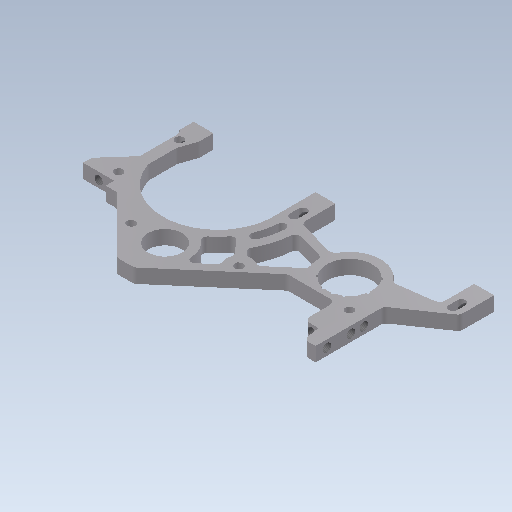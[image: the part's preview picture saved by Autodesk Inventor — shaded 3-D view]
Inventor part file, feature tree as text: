
AUTODESK INVENTOR PART (.ipt)
format: ipt  version: 2020 (Build 240168000, 168)  size: 531,968 bytes
history: native  units: mm (DEFAULTED — no unit token found)
features: sketch x12, hole x8, thread x8, extrude x5, fillet x3, imported_body x1
ambient origin geometry x8: Origin, YZ Plane, XZ Plane, XY Plane, X Axis, Y Axis, Z Axis, Center Point
bodies: Solid1 (feature_tree)
feature tree (37):
  extrude  "Extrusion1"  Depth=2.0mm
  fillet  "Fillet1"  Radius=3.0mm
  extrude  "Extrusion2"  Depth=3.0mm
  fillet  "Fillet2"  Radius=3.0mm
  hole  "Hole1"  [1 undecoded]
  thread  "Thread1"  [1 undecoded]
  hole  "Hole2"  [1 undecoded]
  thread  "Thread2"  [1 undecoded]
  extrude  "Extrusion6"  Depth=1.5mm
  hole  "Hole3"  [1 undecoded]
  thread  "Thread3"  [1 undecoded]
  hole  "Hole4"  [1 undecoded]
  thread  "Thread4"  [1 undecoded]
  hole  "Hole5"  [1 undecoded]
  thread  "Thread5"  [1 undecoded]
  hole  "Hole6"  [1 undecoded]
  thread  "Thread6"  [1 undecoded]
  hole  "Hole7"  [1 undecoded]
  thread  "Thread7"  [1 undecoded]
  hole  "Hole8"  [1 undecoded]
  thread  "Thread8"  [1 undecoded]
  extrude  "Extrusion7"  Depth=10.0mm TaperAngle=0.0deg
  fillet  "Fillet5"  Radius=10.0mm
  extrude  "Extrusion5"  Depth=2.0mm TaperAngle=0.0deg
  sketch  "Sketch3"  dims[d1=10.0mm d2=0.0mm d3=2.0mm d4=3.0mm]
  sketch  "Sketch7"  dims[d8=3.0mm d10=3.0mm d11=3.0mm]
  imported_body  "DerivedBody::500-142"
  sketch  "Sketch8"  dims[d12=3.0mm d13=3.0mm d14=3.0mm]
  sketch  "Sketch9"  dims[d15=3.0mm d17=4.5mm d20=4.5mm]
  sketch  "Sketch10"  dims[d22=10.0mm d23=0.0mm d24=1.5mm]
  sketch  "Sketch11"  dims[d31=26.5mm d32=28.0mm d33=30.0mm]
  sketch  "Sketch13"  dims[d34=2.5mm d35=4.0mm d36=4.0mm]
  sketch  "Sketch14"  dims[d37=4.5mm d38=10.0mm d39=0.0mm]
  sketch  "Sketch15"  dims[d40=3.0mm d41=6.0mm d42=4.0mm d43=2.0mm d44=90.0deg d45=7.5mm d46=20.594885mm d47=7.0mm d48=1.0mm]
  sketch  "Sketch16"  dims[d49=3.0mm d50=6.0mm d51=4.0mm d52=2.0mm d53=90.0deg d54=10.0mm d55=20.594885mm d56=10.0mm d57=0.0mm d58=10.0mm d59=0.0mm]
  sketch  "Sketch17"  dims[d60=3.0mm d61=6.0mm d62=4.0mm d63=2.0mm d64=90.0deg d65=8.0mm d66=20.594885mm d67=10.0mm d68=0.0mm]
  sketch  "Sketch18"  dims[d69=3.0mm d70=6.0mm d71=4.0mm d72=2.0mm d73=90.0deg d74=8.0mm d75=20.594885mm d76=10.0mm d77=0.0mm d78=3.0mm d79=6.0mm d80=4.0mm d81=2.0mm d82=90.0deg d83=6.0mm d84=20.594885mm d85=10.0mm d86=0.0mm d87=3.0mm d88=6.0mm d89=4.0mm d90=2.0mm d91=90.0deg d92=6.0mm d93=20.594885mm d94=10.0mm d95=0.0mm d96=3.0mm d97=6.0mm d98=4.0mm d99=2.0mm d100=90.0deg d101=6.0mm d102=20.594885mm d103=10.0mm d104=0.0mm d105=3.0mm d106=6.0mm d107=4.0mm d108=2.0mm d109=90.0deg d110=6.0mm d111=20.594885mm d112=10.0mm d113=0.0mm d115=6.25mm d116=0.0mm d117=2.0mm]
note: 16 required parameter values undecoded (feature->parameter linkage not recoverable at this tier; creation-order binding heuristic only, values carry confidence <= 0.55)
